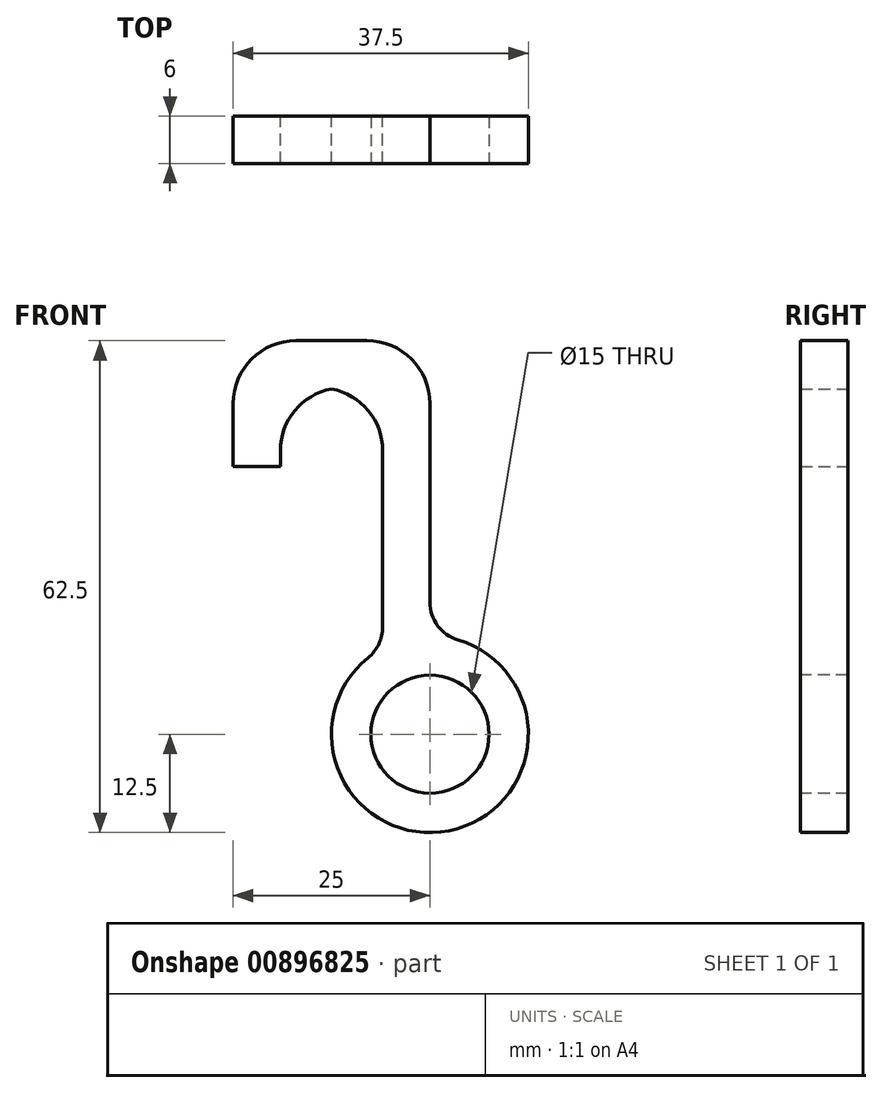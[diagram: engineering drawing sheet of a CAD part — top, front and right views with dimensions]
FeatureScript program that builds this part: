
annotation { "Feature Type Name" : "Feature", "Feature Type Description" : "" }
export const myFeature = defineFeature(function(context is Context, id is Id, definition is map)
    precondition{}
    {
        {
            var Q0;
            Q0=qCreatedBy(makeId("Front.planeOp"),FACE);
            var sketch = newSketch(context, id + "F0", { "sketchPlane" : qUnion([Q0])});
            skLineSegment(sketch, "E0", {"start": v(0, 40) * mm, "end": v(0, 0) * mm});
            skLineSegment(sketch, "E1", {"start": v(0, 0) * mm, "end": v(-6, 0) * mm});
            skLineSegment(sketch, "E2", {"start": v(-6, 0) * mm, "end": v(-6, 34) * mm});
            skLineSegment(sketch, "E3", {"start": v(-19, 34) * mm, "end": v(-6, 34) * mm});
            skLineSegment(sketch, "E4", {"start": v(0, 40) * mm, "end": v(-25, 40) * mm});
            skLineSegment(sketch, "E5", {"start": v(-25, 40) * mm, "end": v(-25, 24) * mm});
            skLineSegment(sketch, "E6", {"start": v(-25, 24) * mm, "end": v(-19, 24) * mm});
            skLineSegment(sketch, "E7", {"start": v(-19, 24) * mm, "end": v(-19, 34) * mm});
            skSolve(sketch);
        }
        {
            var Q0;
            Q0 = qSketchRegion(id + "F0", true);
            extrude(context, id + "F1", {"entities" : qUnion([Q0]), "depth" : 6 * mm, "offsetDistance" : 25 * mm});
        }
        {
            var Q0;
            Q0=qCreatedBy(makeId("Front.planeOp"),FACE);
            var sketch = newSketch(context, id + "F2", { "sketchPlane" : qUnion([Q0])});
            skCircle(sketch, "E8", {"center": v(0, -10) * mm, "radius": 12.5 * mm});
            skSolve(sketch);
        }
        {
            var Q0;
            Q0 = qSketchRegion(id + "F2", true);
            extrude(context, id + "F3", {"entities" : qUnion([Q0]), "operationType" : NewBodyOperationType.ADD, "depth" : 6 * mm, "offsetDistance" : 25 * mm});
        }
        {
            var Q0;
            Q0=makeQuery(id+"F3.boolean.opBoolean","MERGE",FACE,{"derivedFrom":[makeQuery(id+"F1.opExtrude","CAP_FACE",FACE,{"disambiguationData":[OSD([sQuery(id+"F0.wireOp",EDGE,"E0"),sQuery(id+"F0.wireOp",EDGE,"E1"),sQuery(id+"F0.wireOp",EDGE,"E2"),sQuery(id+"F0.wireOp",EDGE,"E3"),sQuery(id+"F0.wireOp",EDGE,"E4"),sQuery(id+"F0.wireOp",EDGE,"E5"),sQuery(id+"F0.wireOp",EDGE,"E6"),sQuery(id+"F0.wireOp",EDGE,"E7")])],"isStart":false}),makeQuery(id+"F3.opExtrude","CAP_FACE",FACE,{"disambiguationData":[OSD([sQuery(id+"F2.wireOp",EDGE,"E8")])],"isStart":false})]});
            var sketch = newSketch(context, id + "F4", { "sketchPlane" : qUnion([Q0])});
            skPoint(sketch, "E9", {"position": v(0, -10) * mm});
            skSolve(sketch);
        }
        {
            var Q0;
            Q0=sQuery(id+"F4.wireOp",VERTEX,"E9");
            var Q1;
            Q1=makeQuery(id+"F1.opExtrude","SWEPT_BODY",BODY,{"disambiguationData":[OSD([sQuery(id+"F0.wireOp",EDGE,"E0"),sQuery(id+"F0.wireOp",EDGE,"E1"),sQuery(id+"F0.wireOp",EDGE,"E2"),sQuery(id+"F0.wireOp",EDGE,"E3"),sQuery(id+"F0.wireOp",EDGE,"E4"),sQuery(id+"F0.wireOp",EDGE,"E5"),sQuery(id+"F0.wireOp",EDGE,"E6"),sQuery(id+"F0.wireOp",EDGE,"E7")])]});
            hole(context, id + "F5", {"style" : HoleStyle.SIMPLE, "endStyle" : HoleEndStyle.THROUGH, "holeDiameter" : 15 * mm, "majorDiameter" : 5 * mm, "isTappedThrough" : true, "tappedDepth" : 12 * mm, "tapClearance" : 3, "startFromSketch" : true, "locations" : qUnion([Q0]), "scope" : qUnion([Q1])});
        }
        {
            var Q0;
            Q0=makeQuery(id+"F1.opExtrude","SWEPT_EDGE",EDGE,{"disambiguationData":[OSD([sQuery(id+"F0.wireOp",EDGE,"E2"),sQuery(id+"F0.wireOp",EDGE,"E3")])]});
            var Q1;
            Q1=makeQuery(id+"F1.opExtrude","SWEPT_EDGE",EDGE,{"disambiguationData":[OSD([sQuery(id+"F0.wireOp",EDGE,"E3"),sQuery(id+"F0.wireOp",EDGE,"E7")])]});
            var Q2;
            Q2=makeQuery(id+"F1.opExtrude","SWEPT_EDGE",EDGE,{"disambiguationData":[OSD([sQuery(id+"F0.wireOp",EDGE,"E0"),sQuery(id+"F0.wireOp",EDGE,"E4")])]});
            var Q3;
            Q3=makeQuery(id+"F1.opExtrude","SWEPT_EDGE",EDGE,{"disambiguationData":[OSD([sQuery(id+"F0.wireOp",EDGE,"E4"),sQuery(id+"F0.wireOp",EDGE,"E5")])]});
            fillet(context, id + "F6", {"entities" : qUnion([Q0, Q1, Q2, Q3]), "radius" : 8 * mm, "tangentPropagation" : true, "allowEdgeOverflow" : false});
        }
        {
            var Q0;
            Q0=makeQuery(id+"F3.boolean.opBoolean","INTERSECT",EDGE,{"derivedFrom":[makeQuery(id+"F1.opExtrude","SWEPT_FACE",FACE,{"disambiguationData":[OSD([sQuery(id+"F0.wireOp",EDGE,"E2")])]}),makeQuery(id+"F3.opExtrude","SWEPT_FACE",FACE,{"disambiguationData":[OSD([sQuery(id+"F2.wireOp",EDGE,"E8")])]})]});
            var Q1;
            Q1=makeQuery(id+"F3.boolean.opBoolean","INTERSECT",EDGE,{"derivedFrom":[makeQuery(id+"F1.opExtrude","SWEPT_FACE",FACE,{"disambiguationData":[OSD([sQuery(id+"F0.wireOp",EDGE,"E0")])]}),makeQuery(id+"F3.opExtrude","SWEPT_FACE",FACE,{"disambiguationData":[OSD([sQuery(id+"F2.wireOp",EDGE,"E8")])]})]});
            fillet(context, id + "F7", {"entities" : qUnion([Q0, Q1]), "radius" : 5 * mm, "tangentPropagation" : true, "allowEdgeOverflow" : false});
        }
    });
